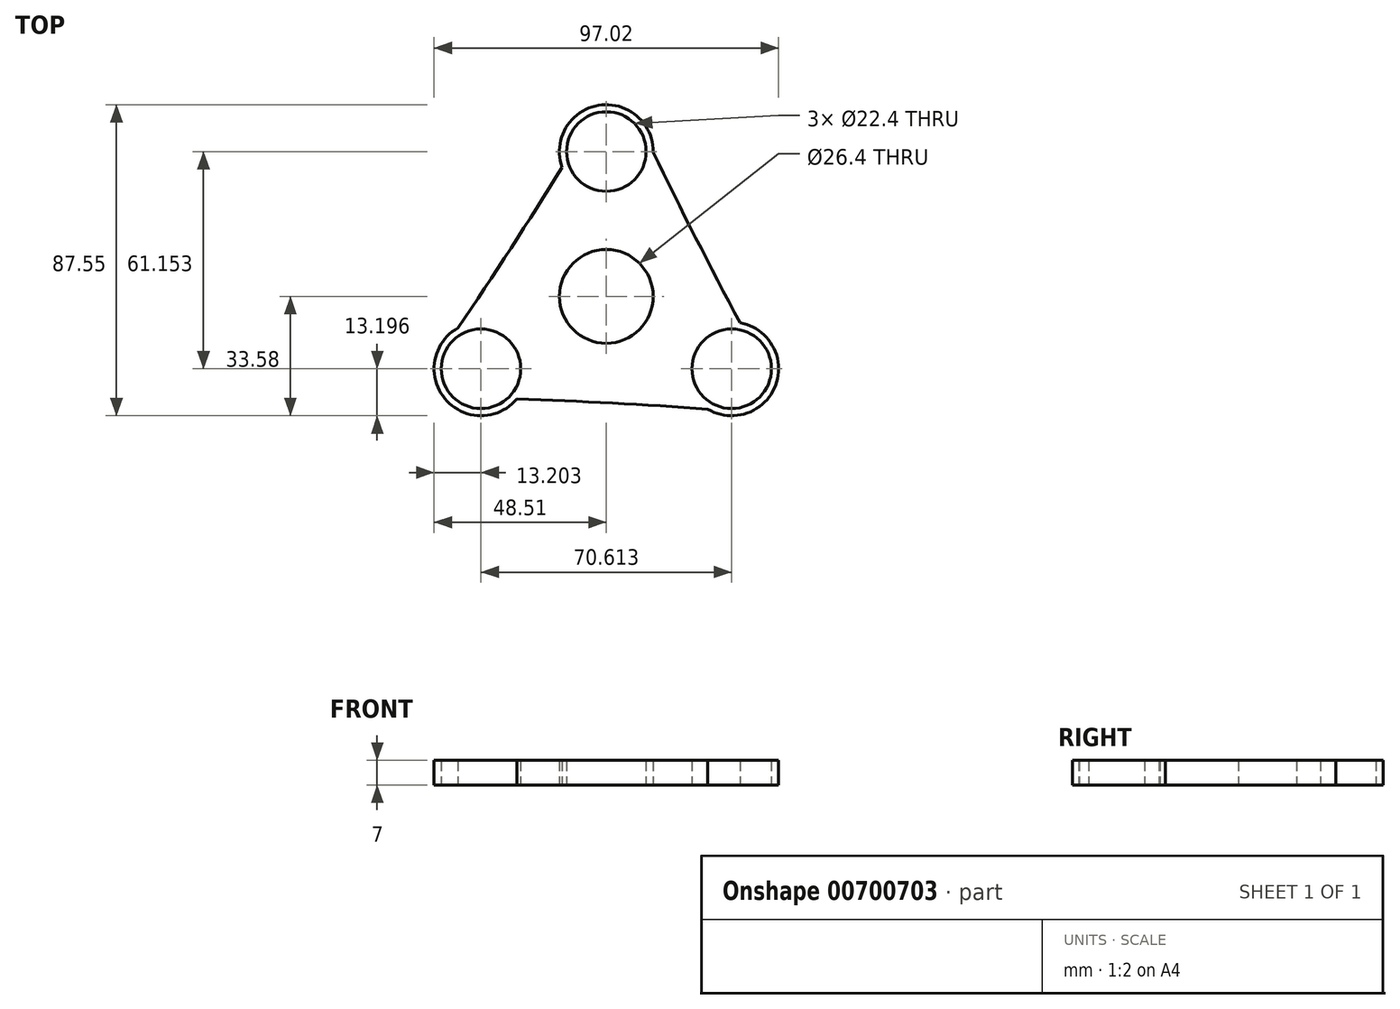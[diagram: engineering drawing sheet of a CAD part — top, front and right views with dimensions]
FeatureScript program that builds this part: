
annotation { "Feature Type Name" : "Feature", "Feature Type Description" : "" }
export const myFeature = defineFeature(function(context is Context, id is Id, definition is map)
    precondition{}
    {
        {
            var Q0;
            Q0=qCreatedBy(makeId("Top.planeOp"),FACE);
            var sketch = newSketch(context, id + "F0", { "sketchPlane" : qUnion([Q0])});
            skCircle(sketch, "E0", {"center": v(0, 0) * mm, "radius": 11.2 * mm});
            skCircle(sketch, "E1", {"center": v(0, 0) * mm, "radius": 13.2 * mm});
            skCircle(sketch, "E2", {"center": v(0, 40.77) * mm, "radius": 11.2 * mm});
            skArc(sketch, "E3", {"start": v(13.2, 40.65) * mm, "mid": v(-2.2, 53.78) * mm, "end": v(-12.43, 36.32) * mm});
            skArc(sketch, "E4.1.0", {"start": v(-41.8, -8.9) * mm, "mid": v(-45.48, -28.8) * mm, "end": v(-25.24, -28.92) * mm});
            skCircle(sketch, "E4.1.1", {"center": v(-35.3, -20.38) * mm, "radius": 11.2 * mm});
            skArc(sketch, "E4.2.0", {"start": v(28.6, -31.75) * mm, "mid": v(47.68, -25) * mm, "end": v(37.67, -7.4) * mm});
            skCircle(sketch, "E4.2.1", {"center": v(35.3, -20.38) * mm, "radius": 11.2 * mm});
            skArc(sketch, "E5", {"start": v(-41.8, -8.9) * mm, "mid": v(-26.87, 13.55) * mm, "end": v(-12.43, 36.32) * mm});
            skArc(sketch, "E6.1.0", {"start": v(28.6, -31.75) * mm, "mid": v(1.7, -30.04) * mm, "end": v(-25.24, -28.92) * mm});
            skArc(sketch, "E6.2.0", {"start": v(13.2, 40.65) * mm, "mid": v(25.17, 16.49) * mm, "end": v(37.67, -7.4) * mm});
            skSolve(sketch);
        }
        {
            var Q0;
            Q0=makeQuery(id+"F0.imprint","IMPRINT",FACE,{"disambiguationData":[TD([[makeQuery(id+"F0.imprint","IMPRINT",EDGE,{"derivedFrom":sQuery(id+"F0.wireOp",EDGE,"E1")}),-1.0]])]});
            extrude(context, id + "F1", {"entities" : qUnion([Q0]), "depth" : 7 * mm, "offsetDistance" : 25 * mm});
        }
    });
